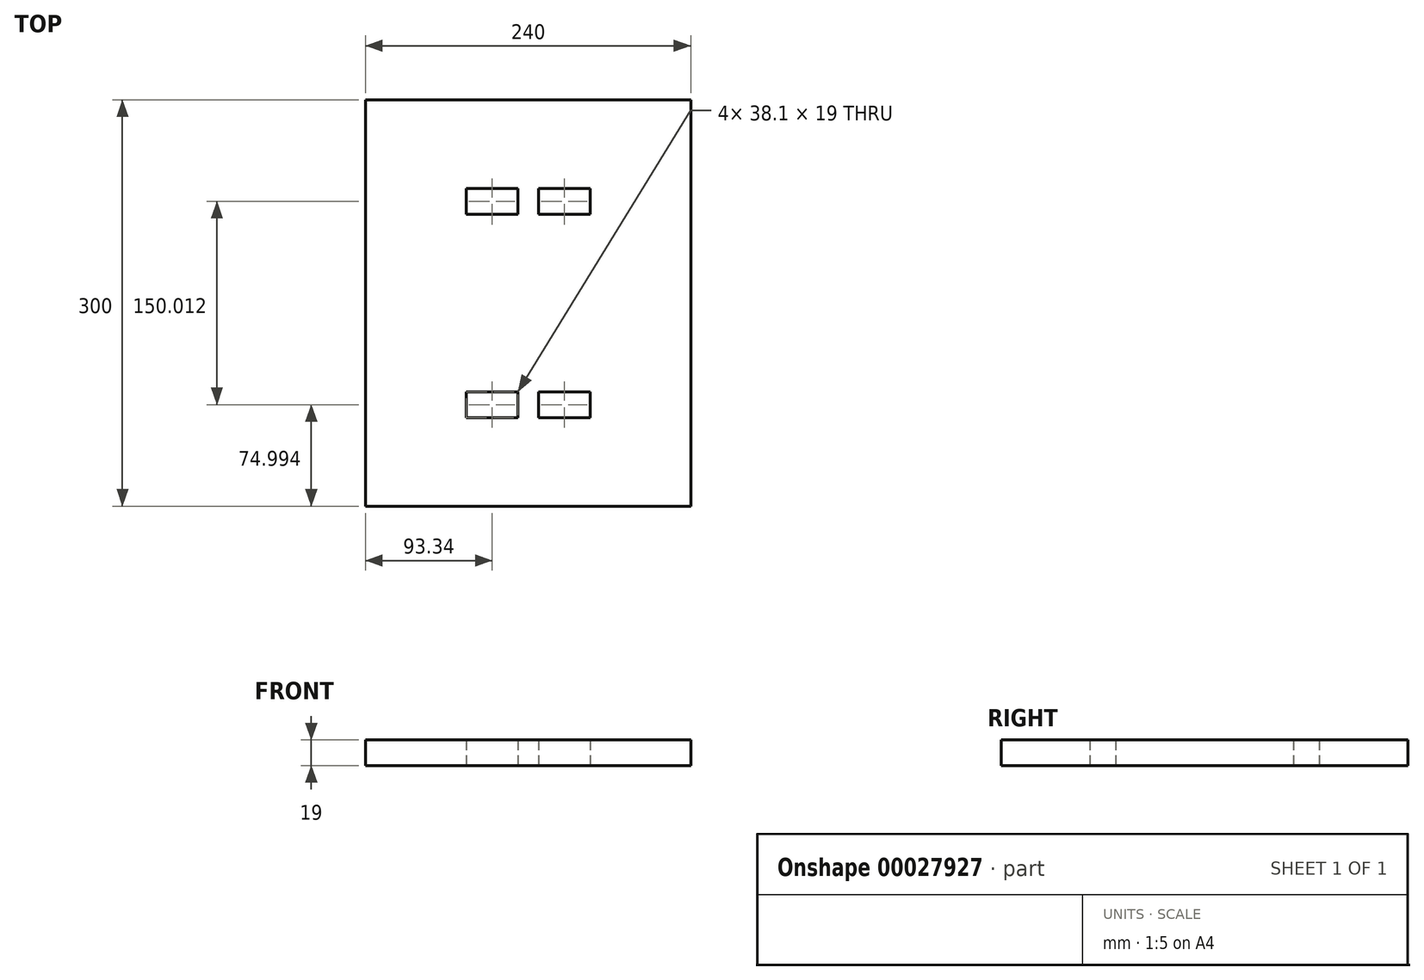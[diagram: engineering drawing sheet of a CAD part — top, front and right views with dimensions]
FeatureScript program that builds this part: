
annotation { "Feature Type Name" : "Feature", "Feature Type Description" : "" }
export const myFeature = defineFeature(function(context is Context, id is Id, definition is map)
    precondition{}
    {
        {
            var Q0;
            Q0=qCreatedBy(makeId("Top.planeOp"),FACE);
            var sketch = newSketch(context, id + "F0", { "sketchPlane" : qUnion([Q0])});
            skLineSegment(sketch, "E0.bottom", {"start": v(0, 0) * mm, "end": v(240, 0) * mm});
            skLineSegment(sketch, "E0.top", {"start": v(0, 300) * mm, "end": v(240, 300) * mm});
            skLineSegment(sketch, "E0.left", {"start": v(0, 0) * mm, "end": v(0, 300) * mm});
            skLineSegment(sketch, "E0.right", {"start": v(240, 0) * mm, "end": v(240, 300) * mm});
            skSolve(sketch);
        }
        {
            var Q0;
            Q0=qSketchRegion(id+"F0",true);
            extrude(context, id + "F1", {"entities" : qUnion([Q0]), "depth" : 19 * mm});
        }
        {
            var Q0;
            Q0=makeQuery(id+"F1.opExtrude","CAP_FACE",FACE,{"disambiguationData":[OSD([sQuery(id+"F0.wireOp",EDGE,"E0.bottom"),sQuery(id+"F0.wireOp",EDGE,"E0.top"),sQuery(id+"F0.wireOp",EDGE,"E0.left"),sQuery(id+"F0.wireOp",EDGE,"E0.right")])],"isStart":true});
            var sketch = newSketch(context, id + "F2", { "sketchPlane" : qUnion([Q0])});
            skLineSegment(sketch, "E1", {"start": v(0, -150) * mm, "end": v(240, -150) * mm});
            skLineSegment(sketch, "E2", {"start": v(240, -75) * mm, "end": v(0, -75) * mm});
            skLineSegment(sketch, "E3", {"start": v(0, -225) * mm, "end": v(240, -225) * mm});
            skLineSegment(sketch, "E4.rect.bottom", {"start": v(112.4, -234.5) * mm, "end": v(74.3, -234.5) * mm});
            skLineSegment(sketch, "E4.rect.top", {"start": v(112.4, -215.5) * mm, "end": v(74.3, -215.5) * mm});
            skLineSegment(sketch, "E4.rect.left", {"start": v(112.4, -234.5) * mm, "end": v(112.4, -215.5) * mm});
            skLineSegment(sketch, "E4.rect.right", {"start": v(74.3, -234.5) * mm, "end": v(74.3, -215.5) * mm});
            skPoint(sketch, "E4.rect.middle", {"position": v(93.34, -225) * mm});
            skLineSegment(sketch, "E5.rect.bottom", {"start": v(165.73, -234.5) * mm, "end": v(127.63, -234.5) * mm});
            skLineSegment(sketch, "E5.rect.top", {"start": v(165.73, -215.5) * mm, "end": v(127.63, -215.5) * mm});
            skLineSegment(sketch, "E5.rect.left", {"start": v(165.73, -234.5) * mm, "end": v(165.73, -215.5) * mm});
            skLineSegment(sketch, "E5.rect.right", {"start": v(127.63, -234.5) * mm, "end": v(127.63, -215.5) * mm});
            skPoint(sketch, "E5.rect.middle", {"position": v(146.68, -225) * mm});
            skLineSegment(sketch, "E6.rect.bottom", {"start": v(165.73, -84.5) * mm, "end": v(127.63, -84.5) * mm});
            skLineSegment(sketch, "E6.rect.top", {"start": v(165.73, -65.5) * mm, "end": v(127.63, -65.5) * mm});
            skLineSegment(sketch, "E6.rect.left", {"start": v(165.73, -84.5) * mm, "end": v(165.73, -65.5) * mm});
            skLineSegment(sketch, "E6.rect.right", {"start": v(127.63, -84.5) * mm, "end": v(127.63, -65.5) * mm});
            skPoint(sketch, "E6.rect.middle", {"position": v(146.68, -75) * mm});
            skLineSegment(sketch, "E7.rect.bottom", {"start": v(112.4, -84.5) * mm, "end": v(74.3, -84.5) * mm});
            skLineSegment(sketch, "E7.rect.top", {"start": v(112.4, -65.5) * mm, "end": v(74.3, -65.5) * mm});
            skLineSegment(sketch, "E7.rect.left", {"start": v(112.4, -84.5) * mm, "end": v(112.4, -65.5) * mm});
            skLineSegment(sketch, "E7.rect.right", {"start": v(74.3, -84.5) * mm, "end": v(74.3, -65.5) * mm});
            skPoint(sketch, "E7.rect.middle", {"position": v(93.34, -75) * mm});
            skSolve(sketch);
        }
        {
            var Q0;
            {var subQ3=sQuery(id+"F2.wireOp",EDGE,"E7.rect.top");Q0=makeQuery(id+"F2.imprint","IMPRINT",FACE,{"disambiguationData":[TD([[makeQuery(id+"F2.imprint","IMPRINT",EDGE,{"derivedFrom":subQ3}),1.0]])]});}
            var Q1;
            {var subQ3=sQuery(id+"F2.wireOp",EDGE,"E7.rect.bottom");Q1=makeQuery(id+"F2.imprint","IMPRINT",FACE,{"disambiguationData":[TD([[makeQuery(id+"F2.imprint","IMPRINT",EDGE,{"derivedFrom":subQ3}),-1.0]])]});}
            var Q2;
            {var subQ3=sQuery(id+"F2.wireOp",EDGE,"E6.rect.top");Q2=makeQuery(id+"F2.imprint","IMPRINT",FACE,{"disambiguationData":[TD([[makeQuery(id+"F2.imprint","IMPRINT",EDGE,{"derivedFrom":subQ3}),1.0]])]});}
            var Q3;
            {var subQ3=sQuery(id+"F2.wireOp",EDGE,"E6.rect.bottom");Q3=makeQuery(id+"F2.imprint","IMPRINT",FACE,{"disambiguationData":[TD([[makeQuery(id+"F2.imprint","IMPRINT",EDGE,{"derivedFrom":subQ3}),-1.0]])]});}
            var Q4;
            {var subQ3=sQuery(id+"F2.wireOp",EDGE,"E5.rect.top");Q4=makeQuery(id+"F2.imprint","IMPRINT",FACE,{"disambiguationData":[TD([[makeQuery(id+"F2.imprint","IMPRINT",EDGE,{"derivedFrom":subQ3}),1.0]])]});}
            var Q5;
            {var subQ3=sQuery(id+"F2.wireOp",EDGE,"E5.rect.bottom");Q5=makeQuery(id+"F2.imprint","IMPRINT",FACE,{"disambiguationData":[TD([[makeQuery(id+"F2.imprint","IMPRINT",EDGE,{"derivedFrom":subQ3}),-1.0]])]});}
            var Q6;
            {var subQ3=sQuery(id+"F2.wireOp",EDGE,"E4.rect.top");Q6=makeQuery(id+"F2.imprint","IMPRINT",FACE,{"disambiguationData":[TD([[makeQuery(id+"F2.imprint","IMPRINT",EDGE,{"derivedFrom":subQ3}),1.0]])]});}
            var Q7;
            {var subQ3=sQuery(id+"F2.wireOp",EDGE,"E4.rect.bottom");Q7=makeQuery(id+"F2.imprint","IMPRINT",FACE,{"disambiguationData":[TD([[makeQuery(id+"F2.imprint","IMPRINT",EDGE,{"derivedFrom":subQ3}),-1.0]])]});}
            extrude(context, id + "F3", {"entities" : qUnion([Q0, Q1, Q2, Q3, Q4, Q5, Q6, Q7]), "operationType" : NewBodyOperationType.REMOVE, "oppositeDirection" : true, "depth" : 19 * mm});
        }
    });
